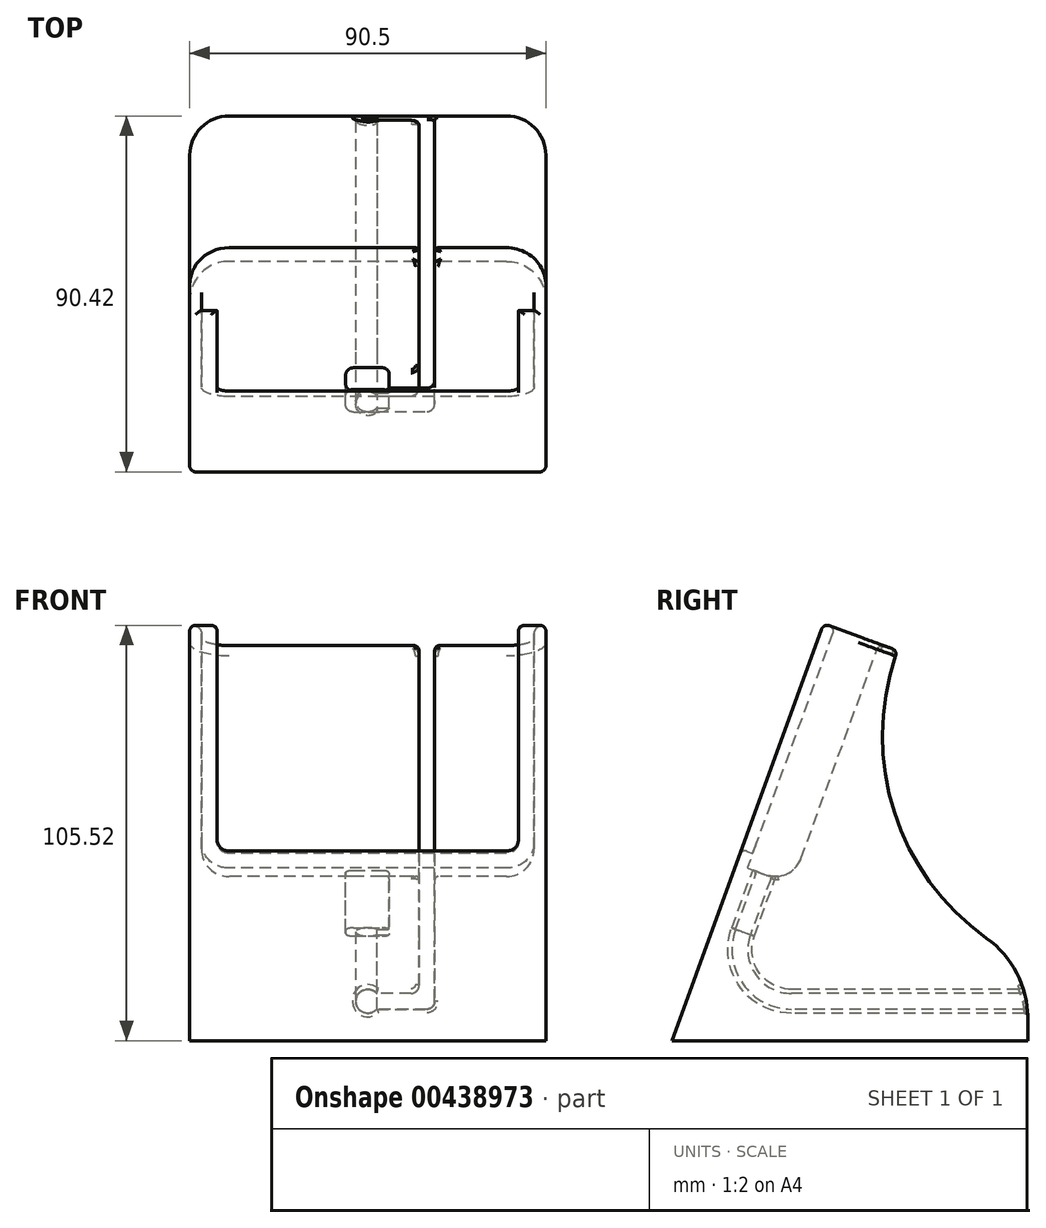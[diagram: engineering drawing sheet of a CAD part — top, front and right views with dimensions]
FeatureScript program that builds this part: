
annotation { "Feature Type Name" : "Feature", "Feature Type Description" : "" }
export const myFeature = defineFeature(function(context is Context, id is Id, definition is map)
    precondition{}
    {
        {
            var Q0;
            Q0=qCreatedBy(makeId("Right.planeOp"),FACE);
            var sketch = newSketch(context, id + "F0", { "sketchPlane" : qUnion([Q0])});
            skLineSegment(sketch, "E0", {"start": v(-11.28, 4.1) * mm, "end": v(-6.58, 2.4) * mm});
            skLineSegment(sketch, "E1", {"start": v(2.4, 6.58) * mm, "end": v(54.72, 150.35) * mm});
            skLineSegment(sketch, "E2", {"start": v(54.72, 150.35) * mm, "end": v(43.45, 154.46) * mm});
            skLineSegment(sketch, "E3", {"start": v(43.45, 154.46) * mm, "end": v(-11.28, 4.1) * mm});
            skPoint(sketch, "E4.visualSharp", {"position": v(0, 0) * mm});
            skArc(sketch, "E4.filletArc", {"start": v(-6.58, 2.4) * mm, "mid": v(-1.23, 2.63) * mm, "end": v(2.4, 6.58) * mm});
            skSolve(sketch);
        }
        {
            var Q0;
            Q0=qSketchRegion(id+"F0",true);
            extrude(context, id + "F1", {"entities" : qUnion([Q0]), "endBound" : BoundingType.SYMMETRIC, "depth" : 84.5 * mm});
        }
        {
            var Q0;
            Q0=makeQuery(id+"F1.opExtrude","CAP_EDGE",EDGE,{"disambiguationData":[OSD([sQuery(id+"F0.wireOp",EDGE,"E1")])],"isStart":false});
            var Q1;
            Q1=makeQuery(id+"F1.opExtrude","CAP_EDGE",EDGE,{"disambiguationData":[OSD([sQuery(id+"F0.wireOp",EDGE,"E1")])],"isStart":true});
            fillet(context, id + "F2", {"entities" : qUnion([Q0, Q1]), "radius" : 7 * mm, "tangentPropagation" : true, "allowEdgeOverflow" : false});
        }
        {
            var Q0;
            Q0=makeQuery(id+"F1.opExtrude","SWEPT_FACE",FACE,{"disambiguationData":[OSD([sQuery(id+"F0.wireOp",EDGE,"E0")])]});
            var sketch = newSketch(context, id + "F3", { "sketchPlane" : qUnion([Q0])});
            skLineSegment(sketch, "E5.bottom", {"start": v(-5.65, 10.5) * mm, "end": v(5.65, 10.5) * mm});
            skLineSegment(sketch, "E5.top", {"start": v(-5.65, 4.4) * mm, "end": v(5.65, 4.4) * mm});
            skLineSegment(sketch, "E5.left", {"start": v(-5.65, 10.5) * mm, "end": v(-5.65, 4.4) * mm});
            skLineSegment(sketch, "E5.right", {"start": v(5.65, 10.5) * mm, "end": v(5.65, 4.4) * mm});
            skLineSegment(sketch, "E6", {"start": v(-5.65, 10.5) * mm, "end": v(5.65, 4.4) * mm});
            skPoint(sketch, "E7", {"position": v(0, 7.45) * mm});
            skSolve(sketch);
        }
        {
            var Q0;
            Q0=qSketchRegion(id+"F3",true);
            extrude(context, id + "F4", {"entities" : qUnion([Q0]), "operationType" : NewBodyOperationType.ADD, "depth" : 15.6 * mm});
        }
        {
            var Q0;
            Q0=qSketchRegion(id+"F3",true);
            var Q1;
            Q1=makeQuery(id+"F1.opExtrude","SWEPT_BODY",BODY,{"disambiguationData":[OSD([sQuery(id+"F0.wireOp",EDGE,"E0"),sQuery(id+"F0.wireOp",EDGE,"E1"),sQuery(id+"F0.wireOp",EDGE,"E2"),sQuery(id+"F0.wireOp",EDGE,"E3"),sQuery(id+"F0.wireOp",EDGE,"E4.filletArc")])]});
            extrude(context, id + "F5", {"entities" : qUnion([Q0]), "operationType" : NewBodyOperationType.ADD, "endBound" : BoundingType.UP_TO_BODY, "oppositeDirection" : true, "endBoundEntityBody" : qUnion([Q1]), "depth" : 25 * mm});
        }
        {
            var Q0;
            Q0=makeQuery(id+"F4.opExtrude","SWEPT_EDGE",EDGE,{"disambiguationData":[OSD([sQuery(id+"F3.wireOp",EDGE,"E5.bottom"),sQuery(id+"F3.wireOp",EDGE,"E5.right")])]});
            var Q1;
            Q1=makeQuery(id+"F4.opExtrude","SWEPT_EDGE",EDGE,{"disambiguationData":[OSD([sQuery(id+"F3.wireOp",EDGE,"E5.top"),sQuery(id+"F3.wireOp",EDGE,"E5.right"),sQuery(id+"F3.wireOp",EDGE,"E6")])]});
            var Q2;
            Q2=makeQuery(id+"F4.opExtrude","SWEPT_EDGE",EDGE,{"disambiguationData":[OSD([sQuery(id+"F3.wireOp",EDGE,"E5.top"),sQuery(id+"F3.wireOp",EDGE,"E5.left")])]});
            var Q3;
            Q3=makeQuery(id+"F4.opExtrude","SWEPT_EDGE",EDGE,{"disambiguationData":[OSD([sQuery(id+"F3.wireOp",EDGE,"E5.bottom"),sQuery(id+"F3.wireOp",EDGE,"E5.left"),sQuery(id+"F3.wireOp",EDGE,"E6")])]});
            fillet(context, id + "F6", {"entities" : qUnion([Q0, Q1, Q2, Q3]), "radius" : 2 * mm, "tangentPropagation" : true, "allowEdgeOverflow" : false});
        }
        {
            var Q0;
            Q0=makeQuery(id+"F4.opExtrude","CAP_FACE",FACE,{"disambiguationData":[OSD([sQuery(id+"F3.wireOp",EDGE,"E5.bottom"),sQuery(id+"F3.wireOp",EDGE,"E5.top"),sQuery(id+"F3.wireOp",EDGE,"E5.left"),sQuery(id+"F3.wireOp",EDGE,"E5.right")])],"isStart":false});
            var sketch = newSketch(context, id + "F7", { "sketchPlane" : qUnion([Q0])});
            skCircle(sketch, "E8", {"center": v(0, 7.45) * mm, "radius": 3.05 * mm});
            skSolve(sketch);
        }
        {
            var Q0;
            {var subQ0=sQuery(id+"F7.wireOp",EDGE,"E8");var subQ1=makeQuery(id+"F7.imprint","INTERSECT",VERTEX,{"derivedFrom":[makeQuery(id+"F4.opExtrude","CAP_EDGE",EDGE,{"disambiguationData":[OSD([sQuery(id+"F3.wireOp",EDGE,"E5.bottom")])],"isStart":false}),subQ0]});Q0=makeQuery(id+"F7.imprint","IMPRINT",FACE,{"disambiguationData":[TD([[makeQuery(id+"F7.imprint","IMPRINT",EDGE,{"disambiguationData":[TD([[subQ1,-1.0]])],"derivedFrom":subQ0}),1.0]])]});}
            var sketch = newSketch(context, id + "F8", { "sketchPlane" : qUnion([Q0])});
            skLineSegment(sketch, "E9", {"start": v(0, 10.5) * mm, "end": v(0, 4.4) * mm});
            skPoint(sketch, "E10", {"position": v(0, 7.45) * mm});
            skSolve(sketch);
        }
        {
            var Q0;
            Q0=qCreatedBy(makeId("Right.planeOp"),FACE);
            var sketch = newSketch(context, id + "F9", { "sketchPlane" : qUnion([Q0])});
            skLineSegment(sketch, "E11", {"start": v(-24.03, -7.86) * mm, "end": v(10.17, -20.3) * mm, "construction": true});
            skArc(sketch, "E12", {"start": v(-12.34, -12.11) * mm, "mid": v(-10.75, -24.13) * mm, "end": v(0, -29.73) * mm});
            skLineSegment(sketch, "E13", {"start": v(0, -16.6) * mm, "end": v(0, -62.2) * mm, "construction": true});
            skSolve(sketch);
        }
        {
            var Q0;
            {var subQ0=sQuery(id+"F8.wireOp",EDGE,"E9");Q0=makeQuery(id+"F8.imprint","IMPRINT",FACE,{"disambiguationData":[TD([[makeQuery(id+"F8.imprint","IMPRINT",EDGE,{"derivedFrom":subQ0}),1.0]])]});}
            var Q1;
            {var subQ0=sQuery(id+"F8.wireOp",EDGE,"E9");Q1=makeQuery(id+"F8.imprint","IMPRINT",FACE,{"disambiguationData":[TD([[makeQuery(id+"F8.imprint","IMPRINT",EDGE,{"derivedFrom":subQ0}),-1.0]])]});}
            var Q2;
            Q2=sQuery(id+"F9.wireOp",EDGE,"E12");
            sweep(context, id + "F10", {"operationType" : NewBodyOperationType.ADD, "profiles" : qUnion([Q0, Q1]), "path" : qUnion([Q2])});
        }
        {
            var Q0;
            Q0=makeQuery(id+"F10.opSweep","CAP_FACE",FACE,{"disambiguationData":[OSD([sQuery(id+"F7.wireOp",EDGE,"E8"),sQuery(id+"F9.wireOp",VERTEX,"E12.end")])],"isStart":false});
            var sketch = newSketch(context, id + "F11", { "sketchPlane" : qUnion([Q0])});
            skCircle(sketch, "E14", {"center": v(0, -29.73) * mm, "radius": 3.05 * mm});
            skSolve(sketch);
        }
        {
            var Q0;
            Q0=qSketchRegion(id+"F11",true);
            extrude(context, id + "F12", {"entities" : qUnion([Q0]), "operationType" : NewBodyOperationType.ADD, "depth" : 60 * mm});
        }
        {
            var Q0;
            Q0=makeQuery(id+"F12.opExtrude","CAP_FACE",FACE,{"disambiguationData":[OSD([sQuery(id+"F11.wireOp",EDGE,"E14")])],"isStart":false});
            var sketch = newSketch(context, id + "F13", { "sketchPlane" : qUnion([Q0])});
            skLineSegment(sketch, "E15", {"start": v(0, -26.68) * mm, "end": v(0, -32.78) * mm});
            skPoint(sketch, "E16", {"position": v(0, -29.73) * mm});
            skSolve(sketch);
        }
        {
            var Q0;
            Q0=qCreatedBy(makeId("Right.planeOp"),FACE);
            var sketch = newSketch(context, id + "F14", { "sketchPlane" : qUnion([Q0])});
            skLineSegment(sketch, "E17", {"start": v(8.14, 66.21) * mm, "end": v(-30.42, -39.73) * mm});
            skLineSegment(sketch, "E18", {"start": v(-30.42, -39.73) * mm, "end": v(60, -39.73) * mm});
            skLineSegment(sketch, "E19", {"start": v(60, -39.73) * mm, "end": v(60, -19.73) * mm});
            skLineSegment(sketch, "E20", {"start": v(60, -19.73) * mm, "end": v(-1.86, -19.73) * mm});
            skLineSegment(sketch, "E21", {"start": v(-1.86, -19.73) * mm, "end": v(26.93, 59.37) * mm});
            skLineSegment(sketch, "E22", {"start": v(26.93, 59.37) * mm, "end": v(8.14, 66.21) * mm});
            skPoint(sketch, "E23", {"position": v(60, -29.73) * mm});
            skSolve(sketch);
        }
        {
            var Q0;
            Q0=qSketchRegion(id+"F14",true);
            extrude(context, id + "F15", {"entities" : qUnion([Q0]), "endBound" : BoundingType.SYMMETRIC, "depth" : (84.5 + 6) * mm});
        }
        {
            var Q0;
            Q0=makeQuery(id+"F1.opExtrude","SWEPT_BODY",BODY,{"disambiguationData":[OSD([sQuery(id+"F0.wireOp",EDGE,"E0"),sQuery(id+"F0.wireOp",EDGE,"E1"),sQuery(id+"F0.wireOp",EDGE,"E2"),sQuery(id+"F0.wireOp",EDGE,"E3"),sQuery(id+"F0.wireOp",EDGE,"E4.filletArc")])]});
            var Q1;
            Q1=makeQuery(id+"F15.opExtrude","SWEPT_BODY",BODY,{"disambiguationData":[OSD([sQuery(id+"F14.wireOp",EDGE,"E17"),sQuery(id+"F14.wireOp",EDGE,"E18"),sQuery(id+"F14.wireOp",EDGE,"E19"),sQuery(id+"F14.wireOp",EDGE,"E20"),sQuery(id+"F14.wireOp",EDGE,"E21"),sQuery(id+"F14.wireOp",EDGE,"E22")])]});
            booleanBodies(context, id + "F16", {"operationType" : BooleanOperationType.SUBTRACTION, "tools" : qUnion([Q0]), "targets" : qUnion([Q1])});
        }
        {
            var Q0;
            Q0=makeQuery(id+"F15.opExtrude","SWEPT_EDGE",EDGE,{"disambiguationData":[OSD([sQuery(id+"F14.wireOp",EDGE,"E20"),sQuery(id+"F14.wireOp",EDGE,"E21")])]});
            fillet(context, id + "F17", {"entities" : qUnion([Q0]), "radius" : 63 * mm, "tangentPropagation" : true, "allowEdgeOverflow" : false});
        }
        {
            var Q0;
            {var subQ0=sQuery(id+"F14.wireOp",EDGE,"E21");var subQ1=sQuery(id+"F14.wireOp",EDGE,"E20");var subQ2=sQuery(id+"F14.wireOp",EDGE,"E19");var subQ3=makeQuery(id+"F15.opExtrude","SWEPT_FACE",FACE,{"disambiguationData":[OSD([subQ2])]});Q0=makeQuery(id+"F21.boolean.opBoolean","SPLIT",EDGE,{"disambiguationData":[TD([makeQuery(id+"F21.opExtrude","CAP_FACE",FACE,{"disambiguationData":[OSD([sQuery(id+"F20.wireOp",EDGE,"E24"),sQuery(id+"F20.wireOp",EDGE,"E27"),sQuery(id+"F20.wireOp",EDGE,"E28"),sQuery(id+"F20.wireOp",EDGE,"E29")])],"isStart":true})])],"derivedFrom":makeQuery(id+"F17.opFillet","BLEND_EDGE",EDGE,{"blendedFrom":[makeQuery(id+"F15.opExtrude","SWEPT_EDGE",EDGE,{"disambiguationData":[OSD([subQ1,subQ0])]}),subQ3],"blendedInto":[subQ3]})});}
            var Q1;
            {var subQ0=sQuery(id+"F14.wireOp",EDGE,"E21");var subQ1=sQuery(id+"F14.wireOp",EDGE,"E20");var subQ2=sQuery(id+"F14.wireOp",EDGE,"E19");var subQ3=makeQuery(id+"F15.opExtrude","SWEPT_FACE",FACE,{"disambiguationData":[OSD([subQ2])]});Q1=makeQuery(id+"F21.boolean.opBoolean","SPLIT",EDGE,{"disambiguationData":[TD([makeQuery(id+"F21.opExtrude","CAP_FACE",FACE,{"disambiguationData":[OSD([sQuery(id+"F20.wireOp",EDGE,"E24"),sQuery(id+"F20.wireOp",EDGE,"E27"),sQuery(id+"F20.wireOp",EDGE,"E28"),sQuery(id+"F20.wireOp",EDGE,"E29")])],"isStart":false})])],"derivedFrom":makeQuery(id+"F17.opFillet","BLEND_EDGE",EDGE,{"blendedFrom":[makeQuery(id+"F15.opExtrude","SWEPT_EDGE",EDGE,{"disambiguationData":[OSD([subQ1,subQ0])]}),subQ3],"blendedInto":[subQ3]})});}
            fillet(context, id + "F18", {"entities" : qUnion([Q0, Q1]), "radius" : 25 * mm, "tangentPropagation" : true, "allowEdgeOverflow" : false});
        }
        {
            var Q0;
            Q0=qCreatedBy(makeId("Right.planeOp"),FACE);
            cPlane(context, id + "F19", {"entities" : qUnion([Q0]), "cplaneType" : CPlaneType.OFFSET, "offset" : 15 * mm, "width" : 150 * mm, "height" : 150 * mm});
        }
        {
            var Q0;
            Q0=qCreatedBy(id+"F19.planeOp",FACE);
            var sketch = newSketch(context, id + "F20", { "sketchPlane" : qUnion([Q0])});
            skArc(sketch, "E24", {"start": v(-12.34, -12.11) * mm, "mid": v(-10.75, -24.13) * mm, "end": v(0, -29.73) * mm});
            skLineSegment(sketch, "E25", {"start": v(-25, -7.5) * mm, "end": v(0, -16.6) * mm, "construction": true});
            skLineSegment(sketch, "E26", {"start": v(0, -16.6) * mm, "end": v(0, -64.6) * mm, "construction": true});
            skLineSegment(sketch, "E27", {"start": v(-12.34, -12.11) * mm, "end": v(24.16, 88.17) * mm});
            skLineSegment(sketch, "E28", {"start": v(0, -29.73) * mm, "end": v(84.4, -29.73) * mm});
            skLineSegment(sketch, "E29", {"start": v(24.16, 88.17) * mm, "end": v(84.4, -29.73) * mm});
            skSolve(sketch);
        }
        {
            var Q0;
            Q0=qSketchRegion(id+"F20",true);
            extrude(context, id + "F21", {"entities" : qUnion([Q0]), "operationType" : NewBodyOperationType.REMOVE, "endBound" : BoundingType.SYMMETRIC, "oppositeDirection" : true, "depth" : 4 * mm});
        }
        {
            var Q0;
            Q0=qCreatedBy(id+"F19.planeOp",FACE);
            var sketch = newSketch(context, id + "F22", { "sketchPlane" : qUnion([Q0])});
            skArc(sketch, "E30", {"start": v(-14.22, -11.43) * mm, "mid": v(-12.4, -25.28) * mm, "end": v(0, -31.73) * mm});
            skArc(sketch, "E31", {"start": v(-10.46, -12.8) * mm, "mid": v(-9.12, -22.98) * mm, "end": v(0, -27.73) * mm});
            skLineSegment(sketch, "E32", {"start": v(-26.25, -7.05) * mm, "end": v(0, -16.6) * mm, "construction": true});
            skLineSegment(sketch, "E33", {"start": v(0, -16.6) * mm, "end": v(0, -59.42) * mm, "construction": true});
            skLineSegment(sketch, "E34", {"start": v(-14.22, -11.43) * mm, "end": v(-4.3, 15.81) * mm});
            skLineSegment(sketch, "E35", {"start": v(-10.46, -12.8) * mm, "end": v(-0.54, 14.45) * mm});
            skLineSegment(sketch, "E36", {"start": v(0, -27.73) * mm, "end": v(65.24, -27.73) * mm});
            skLineSegment(sketch, "E37", {"start": v(65.24, -27.73) * mm, "end": v(65.24, -31.73) * mm});
            skLineSegment(sketch, "E38", {"start": v(65.24, -31.73) * mm, "end": v(0, -31.73) * mm});
            skLineSegment(sketch, "E39", {"start": v(-4.3, 15.81) * mm, "end": v(-0.54, 14.45) * mm});
            skSolve(sketch);
        }
        {
            var Q0;
            Q0=qSketchRegion(id+"F22",true);
            var Q1;
            Q1=qCreatedBy(makeId("Right.planeOp"),FACE);
            extrude(context, id + "F23", {"entities" : qUnion([Q0]), "operationType" : NewBodyOperationType.REMOVE, "endBound" : BoundingType.UP_TO_SURFACE, "oppositeDirection" : true, "endBoundEntityFace" : qUnion([Q1]), "depth" : 25 * mm});
        }
        {
            var Q0;
            Q0=qSketchRegion(id+"F22",true);
            extrude(context, id + "F24", {"entities" : qUnion([Q0]), "operationType" : NewBodyOperationType.REMOVE, "depth" : 2 * mm});
        }
        {
            var Q0;
            Q0=makeQuery(id+"F24.boolean.opBoolean","COPY",EDGE,{"derivedFrom":makeQuery(id+"F24.opExtrude","CAP_EDGE",EDGE,{"disambiguationData":[OSD([sQuery(id+"F22.wireOp",EDGE,"E38")])],"isStart":false})});
            var Q1;
            Q1=makeQuery(id+"F23.boolean.opBoolean","INTERSECT",EDGE,{"derivedFrom":[makeQuery(id+"F21.boolean.opBoolean","COPY",FACE,{"derivedFrom":makeQuery(id+"F21.opExtrude","CAP_FACE",FACE,{"disambiguationData":[OSD([sQuery(id+"F20.wireOp",EDGE,"E24"),sQuery(id+"F20.wireOp",EDGE,"E27"),sQuery(id+"F20.wireOp",EDGE,"E28"),sQuery(id+"F20.wireOp",EDGE,"E29")])],"isStart":false})}),makeQuery(id+"F23.opExtrude","SWEPT_FACE",FACE,{"disambiguationData":[OSD([sQuery(id+"F22.wireOp",EDGE,"E36")])]})]});
            fillet(context, id + "F25", {"entities" : qUnion([Q0, Q1]), "radius" : 2 * mm, "tangentPropagation" : true, "allowEdgeOverflow" : false});
        }
        {
            var Q0;
            Q0=makeQuery(id+"F16.opBoolean","COPY",FACE,{"derivedFrom":makeQuery(id+"F1.opExtrude","SWEPT_FACE",FACE,{"disambiguationData":[OSD([sQuery(id+"F0.wireOp",EDGE,"E3")])]})});
            var sketch = newSketch(context, id + "F26", { "sketchPlane" : qUnion([Q0])});
            skLineSegment(sketch, "E40.0", {"start": v(38.25, 65) * mm, "end": v(38.25, 7) * mm});
            skLineSegment(sketch, "E40.1", {"start": v(-38.25, 65) * mm, "end": v(-38.25, 7) * mm});
            skArc(sketch, "E40.2", {"start": v(-35.25, 4) * mm, "mid": v(-37.37, 4.88) * mm, "end": v(-38.25, 7) * mm});
            skLineSegment(sketch, "E40.3", {"start": v(-35.25, 4) * mm, "end": v(35.25, 4) * mm});
            skArc(sketch, "E40.4", {"start": v(38.25, 7) * mm, "mid": v(37.37, 4.88) * mm, "end": v(35.25, 4) * mm});
            skLineSegment(sketch, "E41", {"start": v(-38.25, 65) * mm, "end": v(38.25, 65) * mm});
            skSolve(sketch);
        }
        {
            var Q0;
            Q0=qSketchRegion(id+"F26",true);
            extrude(context, id + "F27", {"entities" : qUnion([Q0]), "operationType" : NewBodyOperationType.REMOVE, "endBound" : BoundingType.THROUGH_ALL, "oppositeDirection" : true, "depth" : 25 * mm});
        }
        {
            var Q0;
            Q0=makeQuery(id+"F15.opExtrude","CAP_EDGE",EDGE,{"disambiguationData":[OSD([sQuery(id+"F14.wireOp",EDGE,"E17")])],"isStart":false});
            var Q1;
            Q1=makeQuery(id+"F15.opExtrude","CAP_EDGE",EDGE,{"disambiguationData":[OSD([sQuery(id+"F14.wireOp",EDGE,"E17")])],"isStart":true});
            var Q2;
            {var subQ0=sQuery(id+"F14.wireOp",EDGE,"E17");var subQ1=sQuery(id+"F14.wireOp",EDGE,"E22");Q2=makeQuery(id+"F27.boolean.opBoolean","SPLIT",EDGE,{"disambiguationData":[TD([makeQuery(id+"F27.opExtrude","SWEPT_FACE",FACE,{"disambiguationData":[OSD([sQuery(id+"F26.wireOp",EDGE,"E40.0")])]})])],"derivedFrom":makeQuery(id+"F15.opExtrude","SWEPT_EDGE",EDGE,{"disambiguationData":[OSD([subQ0,subQ1])]})});}
            var Q3;
            {var subQ0=sQuery(id+"F14.wireOp",EDGE,"E17");var subQ1=sQuery(id+"F14.wireOp",EDGE,"E22");Q3=makeQuery(id+"F27.boolean.opBoolean","SPLIT",EDGE,{"disambiguationData":[TD([makeQuery(id+"F27.opExtrude","SWEPT_FACE",FACE,{"disambiguationData":[OSD([sQuery(id+"F26.wireOp",EDGE,"E40.1")])]})])],"derivedFrom":makeQuery(id+"F15.opExtrude","SWEPT_EDGE",EDGE,{"disambiguationData":[OSD([subQ0,subQ1])]})});}
            var Q4;
            Q4=makeQuery(id+"F27.boolean.opBoolean","INTERSECT",EDGE,{"derivedFrom":[makeQuery(id+"F15.opExtrude","SWEPT_FACE",FACE,{"disambiguationData":[OSD([sQuery(id+"F14.wireOp",EDGE,"E17")])]}),makeQuery(id+"F27.opExtrude","SWEPT_FACE",FACE,{"disambiguationData":[OSD([sQuery(id+"F26.wireOp",EDGE,"E40.1")])]})]});
            var Q5;
            {var subQ2=sQuery(id+"F14.wireOp",EDGE,"E22");Q5=makeQuery(id+"F27.boolean.opBoolean","SPLIT",FACE,{"disambiguationData":[TD([makeQuery(id+"F27.opExtrude","SWEPT_FACE",FACE,{"disambiguationData":[OSD([sQuery(id+"F26.wireOp",EDGE,"E40.0")])]})])],"derivedFrom":makeQuery(id+"F15.opExtrude","SWEPT_FACE",FACE,{"disambiguationData":[OSD([subQ2])]})});}
            var Q6;
            {var subQ2=sQuery(id+"F14.wireOp",EDGE,"E22");Q6=makeQuery(id+"F27.boolean.opBoolean","SPLIT",FACE,{"disambiguationData":[TD([makeQuery(id+"F27.opExtrude","SWEPT_FACE",FACE,{"disambiguationData":[OSD([sQuery(id+"F26.wireOp",EDGE,"E40.1")])]})])],"derivedFrom":makeQuery(id+"F15.opExtrude","SWEPT_FACE",FACE,{"disambiguationData":[OSD([subQ2])]})});}
            fillet(context, id + "F28", {"entities" : qUnion([Q0, Q1, Q2, Q3, Q4, Q5, Q6]), "radius" : 1.5 * mm, "tangentPropagation" : true, "allowEdgeOverflow" : false});
        }
        {
            var Q0;
            {var subQ0=sQuery(id+"F14.wireOp",EDGE,"E21");var subQ1=sQuery(id+"F14.wireOp",EDGE,"E20");Q0=makeQuery(id+"F17.opFillet","BLEND_EDGE",EDGE,{"blendedFrom":[makeQuery(id+"F15.opExtrude","SWEPT_EDGE",EDGE,{"disambiguationData":[OSD([subQ1,subQ0])]}),makeQuery(id+"F15.opExtrude","CAP_FACE",FACE,{"disambiguationData":[OSD([sQuery(id+"F14.wireOp",EDGE,"E17"),sQuery(id+"F14.wireOp",EDGE,"E18"),sQuery(id+"F14.wireOp",EDGE,"E19"),subQ1,subQ0,sQuery(id+"F14.wireOp",EDGE,"E22")])],"isStart":true})],"blendedInto":[makeQuery(id+"F15.opExtrude","CAP_FACE",FACE,{"disambiguationData":[OSD([sQuery(id+"F14.wireOp",EDGE,"E17"),sQuery(id+"F14.wireOp",EDGE,"E18"),sQuery(id+"F14.wireOp",EDGE,"E19"),subQ1,subQ0,sQuery(id+"F14.wireOp",EDGE,"E22")])],"isStart":true})]});}
            var Q1;
            {var subQ0=sQuery(id+"F14.wireOp",EDGE,"E21");var subQ1=sQuery(id+"F14.wireOp",EDGE,"E20");Q1=makeQuery(id+"F17.opFillet","BLEND_EDGE",EDGE,{"blendedFrom":[makeQuery(id+"F15.opExtrude","SWEPT_EDGE",EDGE,{"disambiguationData":[OSD([subQ1,subQ0])]}),makeQuery(id+"F15.opExtrude","CAP_FACE",FACE,{"disambiguationData":[OSD([sQuery(id+"F14.wireOp",EDGE,"E17"),sQuery(id+"F14.wireOp",EDGE,"E18"),sQuery(id+"F14.wireOp",EDGE,"E19"),subQ1,subQ0,sQuery(id+"F14.wireOp",EDGE,"E22")])],"isStart":false})],"blendedInto":[makeQuery(id+"F15.opExtrude","CAP_FACE",FACE,{"disambiguationData":[OSD([sQuery(id+"F14.wireOp",EDGE,"E17"),sQuery(id+"F14.wireOp",EDGE,"E18"),sQuery(id+"F14.wireOp",EDGE,"E19"),subQ1,subQ0,sQuery(id+"F14.wireOp",EDGE,"E22")])],"isStart":false})]});}
            fillet(context, id + "F29", {"entities" : qUnion([Q0, Q1]), "radius" : 10 * mm, "tangentPropagation" : true, "allowEdgeOverflow" : false});
        }
        {
            var Q0;
            Q0=makeQuery(id+"F21.boolean.opBoolean","INTERSECT",EDGE,{"derivedFrom":[makeQuery(id+"F17.opFillet","BLEND_FACE",FACE,{"disambiguationData":[OSD([sQuery(id+"F14.wireOp",EDGE,"E20"),sQuery(id+"F14.wireOp",EDGE,"E21")])]}),makeQuery(id+"F21.opExtrude","CAP_FACE",FACE,{"disambiguationData":[OSD([sQuery(id+"F20.wireOp",EDGE,"E24"),sQuery(id+"F20.wireOp",EDGE,"E27"),sQuery(id+"F20.wireOp",EDGE,"E28"),sQuery(id+"F20.wireOp",EDGE,"E29")])],"isStart":false})]});
            var Q1;
            Q1=makeQuery(id+"F21.boolean.opBoolean","INTERSECT",EDGE,{"derivedFrom":[makeQuery(id+"F17.opFillet","BLEND_FACE",FACE,{"disambiguationData":[OSD([sQuery(id+"F14.wireOp",EDGE,"E20"),sQuery(id+"F14.wireOp",EDGE,"E21")])]}),makeQuery(id+"F21.opExtrude","CAP_FACE",FACE,{"disambiguationData":[OSD([sQuery(id+"F20.wireOp",EDGE,"E24"),sQuery(id+"F20.wireOp",EDGE,"E27"),sQuery(id+"F20.wireOp",EDGE,"E28"),sQuery(id+"F20.wireOp",EDGE,"E29")])],"isStart":true})]});
            var Q2;
            Q2=makeQuery(id+"F18.opFillet","BLEND_EDGE",EDGE,{"blendedFrom":[makeQuery(id+"F17.opFillet","BLEND_EDGE",EDGE,{"blendedFrom":[makeQuery(id+"F15.opExtrude","SWEPT_EDGE",EDGE,{"disambiguationData":[OSD([sQuery(id+"F14.wireOp",EDGE,"E20"),sQuery(id+"F14.wireOp",EDGE,"E21")])]}),makeQuery(id+"F15.opExtrude","SWEPT_FACE",FACE,{"disambiguationData":[OSD([sQuery(id+"F14.wireOp",EDGE,"E19")])]})],"blendedInto":[makeQuery(id+"F15.opExtrude","SWEPT_FACE",FACE,{"disambiguationData":[OSD([sQuery(id+"F14.wireOp",EDGE,"E19")])]})]}),makeQuery(id+"F16.opBoolean","COPY",FACE,{"derivedFrom":makeQuery(id+"F12.opExtrude","SWEPT_FACE",FACE,{"disambiguationData":[OSD([sQuery(id+"F11.wireOp",EDGE,"E14")])]})})],"blendedInto":[makeQuery(id+"F16.opBoolean","COPY",FACE,{"derivedFrom":makeQuery(id+"F12.opExtrude","SWEPT_FACE",FACE,{"disambiguationData":[OSD([sQuery(id+"F11.wireOp",EDGE,"E14")])]})})]});
            var Q3;
            Q3=makeQuery(id+"F21.boolean.opBoolean","INTERSECT",EDGE,{"derivedFrom":[makeQuery(id+"F16.opBoolean","COPY",FACE,{"derivedFrom":makeQuery(id+"F1.opExtrude","SWEPT_FACE",FACE,{"disambiguationData":[OSD([sQuery(id+"F0.wireOp",EDGE,"E1")])]})}),makeQuery(id+"F21.opExtrude","CAP_FACE",FACE,{"disambiguationData":[OSD([sQuery(id+"F20.wireOp",EDGE,"E24"),sQuery(id+"F20.wireOp",EDGE,"E27"),sQuery(id+"F20.wireOp",EDGE,"E28"),sQuery(id+"F20.wireOp",EDGE,"E29")])],"isStart":false})]});
            var Q4;
            Q4=makeQuery(id+"F21.boolean.opBoolean","INTERSECT",EDGE,{"derivedFrom":[makeQuery(id+"F16.opBoolean","COPY",FACE,{"derivedFrom":makeQuery(id+"F1.opExtrude","SWEPT_FACE",FACE,{"disambiguationData":[OSD([sQuery(id+"F0.wireOp",EDGE,"E1")])]})}),makeQuery(id+"F21.opExtrude","CAP_FACE",FACE,{"disambiguationData":[OSD([sQuery(id+"F20.wireOp",EDGE,"E24"),sQuery(id+"F20.wireOp",EDGE,"E27"),sQuery(id+"F20.wireOp",EDGE,"E28"),sQuery(id+"F20.wireOp",EDGE,"E29")])],"isStart":true})]});
            var Q5;
            {var subQ0=sQuery(id+"F3.wireOp",EDGE,"E5.left");Q5=makeQuery(id+"F16.opBoolean","COPY",EDGE,{"derivedFrom":makeQuery(id+"F4.boolean.opBoolean","SPLIT",EDGE,{"disambiguationData":[topologyDisambiguationEdgeConnected([makeQuery(id+"F1.opExtrude","SWEPT_FACE",FACE,{"disambiguationData":[OSD([sQuery(id+"F0.wireOp",EDGE,"E0")])]})])],"derivedFrom":makeQuery(id+"F4.opExtrude","CAP_EDGE",EDGE,{"disambiguationData":[OSD([subQ0])],"isStart":true})})});}
            fillet(context, id + "F30", {"entities" : qUnion([Q0, Q1, Q2, Q3, Q4, Q5]), "radius" : .9 * mm, "tangentPropagation" : true, "allowEdgeOverflow" : false});
        }
    });
